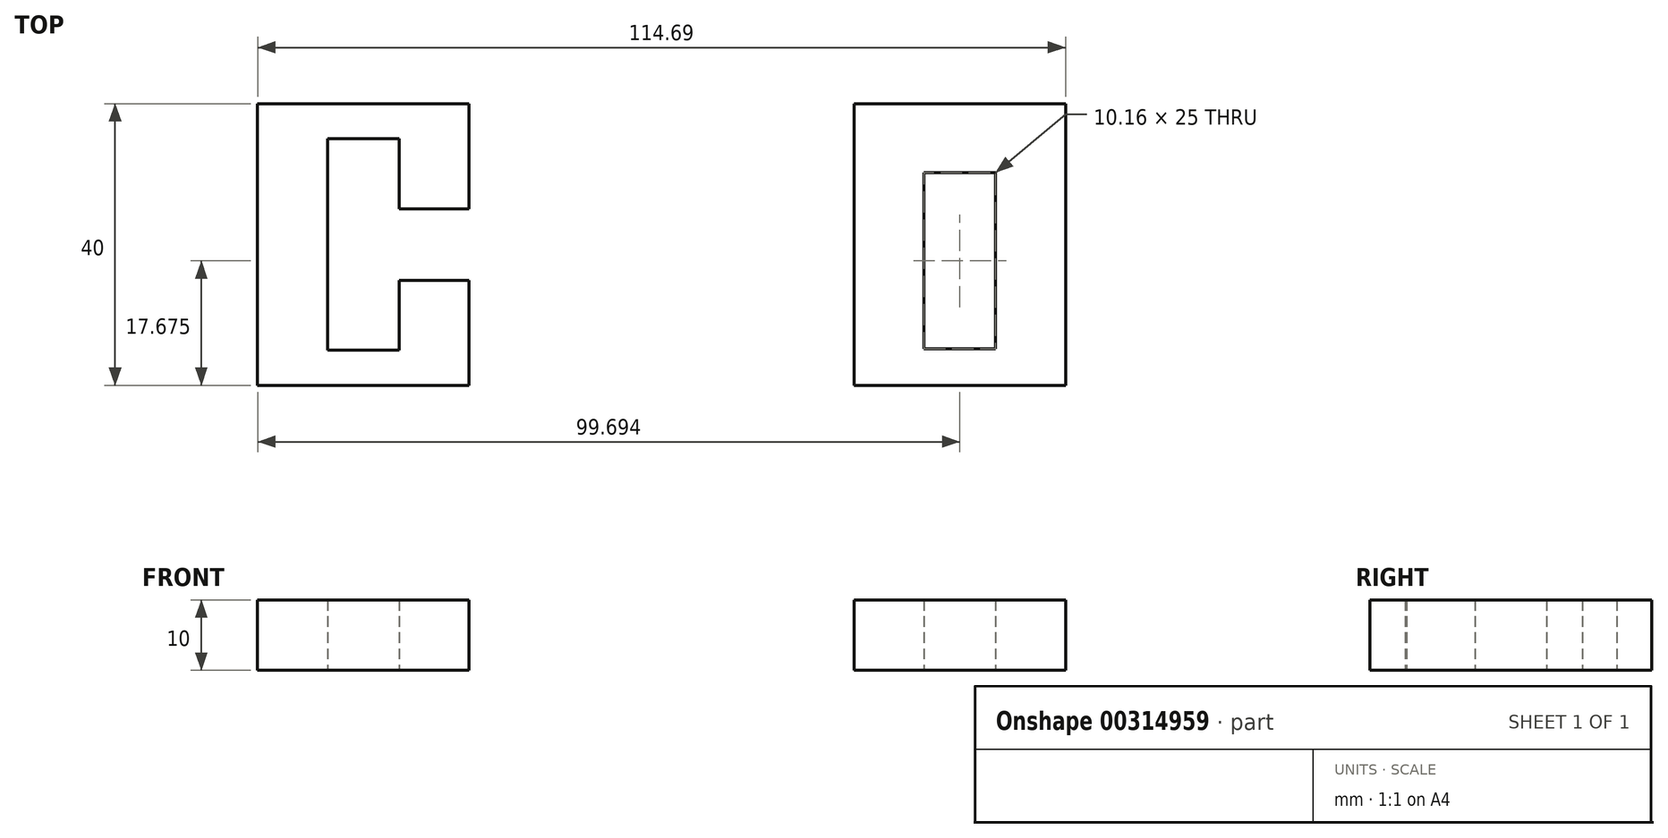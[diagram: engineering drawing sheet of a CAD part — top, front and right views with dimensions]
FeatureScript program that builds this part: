
annotation { "Feature Type Name" : "Feature", "Feature Type Description" : "" }
export const myFeature = defineFeature(function(context is Context, id is Id, definition is map)
    precondition{}
    {
        {
            var Q0;
            Q0=qCreatedBy(makeId("Top.planeOp"),FACE);
            var sketch = newSketch(context, id + "F0", { "sketchPlane" : qUnion([Q0])});
            skLineSegment(sketch, "E0", {"start": v(-51.25, 46.87) * mm, "end": v(-81.25, 46.87) * mm});
            skLineSegment(sketch, "E1", {"start": v(-81.25, 46.87) * mm, "end": v(-81.25, 6.87) * mm});
            skLineSegment(sketch, "E2", {"start": v(-81.25, 6.87) * mm, "end": v(-51.25, 6.87) * mm});
            skLineSegment(sketch, "E3", {"start": v(-51.25, 6.87) * mm, "end": v(-51.25, 21.8) * mm});
            skLineSegment(sketch, "E4", {"start": v(-51.25, 21.8) * mm, "end": v(-61.17, 21.8) * mm});
            skLineSegment(sketch, "E5", {"start": v(-61.17, 21.8) * mm, "end": v(-61.17, 11.87) * mm});
            skLineSegment(sketch, "E6", {"start": v(-61.17, 11.87) * mm, "end": v(-71.33, 11.87) * mm});
            skLineSegment(sketch, "E7", {"start": v(-71.33, 11.87) * mm, "end": v(-71.33, 41.87) * mm});
            skLineSegment(sketch, "E8", {"start": v(-71.33, 41.87) * mm, "end": v(-61.17, 41.87) * mm});
            skLineSegment(sketch, "E9", {"start": v(-61.17, 41.87) * mm, "end": v(-61.17, 31.95) * mm});
            skLineSegment(sketch, "E10", {"start": v(-61.17, 31.95) * mm, "end": v(-51.25, 31.95) * mm});
            skLineSegment(sketch, "E11", {"start": v(-51.25, 31.95) * mm, "end": v(-51.25, 46.87) * mm});
            skLineSegment(sketch, "E12", {"start": v(3.44, 46.87) * mm, "end": v(3.44, 6.87) * mm});
            skLineSegment(sketch, "E13", {"start": v(3.44, 6.87) * mm, "end": v(33.44, 6.87) * mm});
            skLineSegment(sketch, "E14", {"start": v(33.44, 6.87) * mm, "end": v(33.44, 46.87) * mm});
            skLineSegment(sketch, "E15", {"start": v(33.44, 46.87) * mm, "end": v(3.44, 46.87) * mm});
            skLineSegment(sketch, "E16.bottom", {"start": v(13.36, 37.04) * mm, "end": v(23.52, 37.04) * mm});
            skLineSegment(sketch, "E16.top", {"start": v(13.36, 12.04) * mm, "end": v(23.52, 12.04) * mm});
            skLineSegment(sketch, "E16.left", {"start": v(13.36, 37.04) * mm, "end": v(13.36, 12.04) * mm});
            skLineSegment(sketch, "E16.right", {"start": v(23.52, 37.04) * mm, "end": v(23.52, 12.04) * mm});
            skLineSegment(sketch, "E17", {"start": v(-64.64, 41.87) * mm, "end": v(-64.64, 46.87) * mm, "construction": true});
            skLineSegment(sketch, "E18", {"start": v(-63.88, 6.87) * mm, "end": v(-63.88, 11.87) * mm, "construction": true});
            skLineSegment(sketch, "E19", {"start": v(-81.25, 12.79) * mm, "end": v(-71.33, 12.79) * mm, "construction": true});
            skLineSegment(sketch, "E20", {"start": v(-61.17, 16.83) * mm, "end": v(-51.25, 16.83) * mm, "construction": true});
            skLineSegment(sketch, "E21", {"start": v(3.44, 36.5) * mm, "end": v(13.36, 36.5) * mm, "construction": true});
            skLineSegment(sketch, "E22", {"start": v(23.52, 36.17) * mm, "end": v(33.44, 36.17) * mm, "construction": true});
            skSolve(sketch);
        }
        {
            var Q0;
            Q0=makeQuery(id+"F0.imprint","IMPRINT",FACE,{"disambiguationData":[TD([[makeQuery(id+"F0.imprint","IMPRINT",EDGE,{"derivedFrom":sQuery(id+"F0.wireOp",EDGE,"E0")}),1.0]])]});
            var Q1;
            Q1=makeQuery(id+"F0.imprint","IMPRINT",FACE,{"disambiguationData":[TD([[makeQuery(id+"F0.imprint","IMPRINT",EDGE,{"derivedFrom":sQuery(id+"F0.wireOp",EDGE,"E12")}),1.0]])]});
            extrude(context, id + "F1", {"entities" : qUnion([Q0, Q1]), "depth" : 10 * mm});
        }
    });
